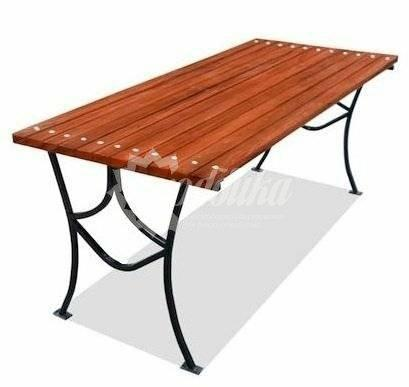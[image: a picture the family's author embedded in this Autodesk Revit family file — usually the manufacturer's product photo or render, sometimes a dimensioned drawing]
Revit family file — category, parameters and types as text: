
# Revit family: 6692 Стол садовый «Элегант» Хоббика
name_source: partatom
category: Антураж
revit_build: Autodesk Revit 2018 (Build: 20180423_1000(x64)
units: mm (PartAtom-declared; Revit-internal decimal feet)

## family parameters
Всегда вертикально = Да
Источник визуального образа = Геометрия семейства
На основе рабочей плоскости = Нет
Общий = Нет
При загрузке вырезать с полостями = Нет
Точка расчета площади = Нет

## types (6) — shared parameters
URL = https://hobbyka.ru
Артикул товара = Арт. 6722
Высота = 780 мм
Группа модели = Садовые столы
Изготовитель = ООО «Хоббика»
Изображение типоразмера = Стол садовый «Элегант» Арт 6692.jpg
Материал изделия = Сталь, дерево
Средняя опора = Да
Цвет опор = Сталь
Цвет столешници = Дерево
Ширна = 710 мм

## per-type parameters (varying)
| type | Версия 1,2 м | Версия 1,5 м | Версия 1,8 м | Версия 2,0 м | Версия 2,5 м | Версия 3,0 м | Длина | Описание |
| Версия 1,2 м | Да | Нет | Нет | Нет | Да | Нет | 1200 мм | Стол садовый «Элегант». Версия 1,2 м |
| Версия 1,5 м | Нет | Да | Нет | Нет | Да | Нет | 1500 мм | Стол садовый «Элегант». Версия 1,5 м |
| Версия 1,8 м | Нет | Нет | Да | Нет | Да | Нет | 1800 мм | Стол садовый «Элегант». Версия 1,8 м |
| Версия 2,0 м | Нет | Нет | Нет | Да | Да | Нет | 2000 мм | Стол садовый «Элегант». Версия 2,0 м |
| Версия 3,0 м | Нет | Нет | Нет | Нет | Нет | Да | 3000 мм | Стол садовый «Элегант». Версия 3,0 м |
| Версия 2,5 м | Нет | Нет | Нет | Нет | Да | Нет | 2500 мм | Стол садовый «Элегант». Версия 2,5 м |
